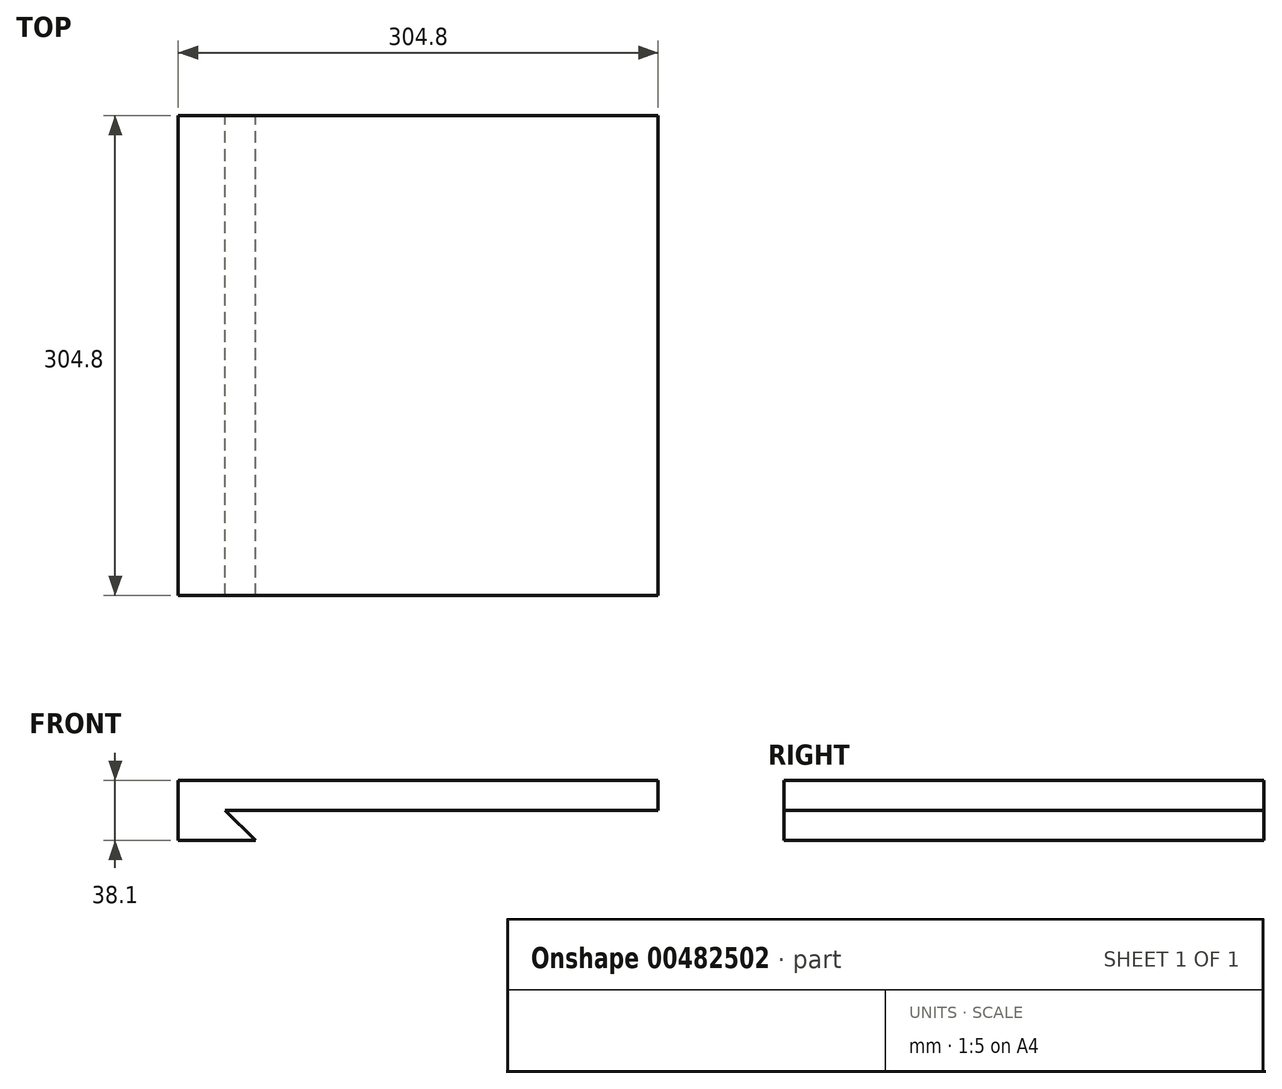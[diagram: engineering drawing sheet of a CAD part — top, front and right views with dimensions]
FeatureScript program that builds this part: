
annotation { "Feature Type Name" : "Feature", "Feature Type Description" : "" }
export const myFeature = defineFeature(function(context is Context, id is Id, definition is map)
    precondition{}
    {
        {
            var Q0;
            Q0=qCreatedBy(makeId("Front.planeOp"),FACE);
            var sketch = newSketch(context, id + "F0", { "sketchPlane" : qUnion([Q0])});
            skLineSegment(sketch, "E0.bottom", {"start": v(-148.7, -0.93) * mm, "end": v(156.1, -0.93) * mm});
            skLineSegment(sketch, "E0.top", {"start": v(-148.7, -19.98) * mm, "end": v(156.1, -19.98) * mm});
            skLineSegment(sketch, "E0.left", {"start": v(-148.7, -0.93) * mm, "end": v(-148.7, -19.98) * mm});
            skLineSegment(sketch, "E0.right", {"start": v(156.1, -0.93) * mm, "end": v(156.1, -19.98) * mm});
            skLineSegment(sketch, "E1", {"start": v(-148.7, -19.98) * mm, "end": v(-148.7, -39.03) * mm});
            skLineSegment(sketch, "E2", {"start": v(-148.7, -39.03) * mm, "end": v(-99.6, -39.03) * mm});
            skLineSegment(sketch, "E3", {"start": v(-99.6, -39.03) * mm, "end": v(-119.1, -19.98) * mm});
            skLineSegment(sketch, "E4.bottom", {"start": v(156.1, -19.98) * mm, "end": v(-44.68, -19.98) * mm});
            skLineSegment(sketch, "E4.top", {"start": v(156.1, -39.03) * mm, "end": v(-44.68, -39.03) * mm});
            skLineSegment(sketch, "E4.left", {"start": v(156.1, -19.98) * mm, "end": v(156.1, -39.03) * mm});
            skLineSegment(sketch, "E4.right", {"start": v(-44.68, -19.98) * mm, "end": v(-44.68, -39.03) * mm});
            skSolve(sketch);
        }
        {
            var Q0;
            {var subQ0=sQuery(id+"F0.wireOp",EDGE,"E1");Q0=makeQuery(id+"F0.imprint","IMPRINT",FACE,{"disambiguationData":[TD([[makeQuery(id+"F0.imprint","IMPRINT",EDGE,{"derivedFrom":subQ0}),1.0]])]});}
            var Q1;
            Q1=makeQuery(id+"F0.imprint","IMPRINT",FACE,{"disambiguationData":[TD([[makeQuery(id+"F0.imprint","IMPRINT",EDGE,{"derivedFrom":sQuery(id+"F0.wireOp",EDGE,"E0.bottom")}),-1.0]])]});
            var Q2;
            Q2=makeQuery(id+"F0.imprint","IMPRINT",FACE,{"disambiguationData":[TD([[makeQuery(id+"F0.imprint","IMPRINT",EDGE,{"derivedFrom":sQuery(id+"F0.wireOp",EDGE,"E4.bottom")}),1.0]])]});
            extrude(context, id + "F1", {"entities" : qUnion([Q0, Q1, Q2]), "depth" : 304.8 * mm});
        }
    });
